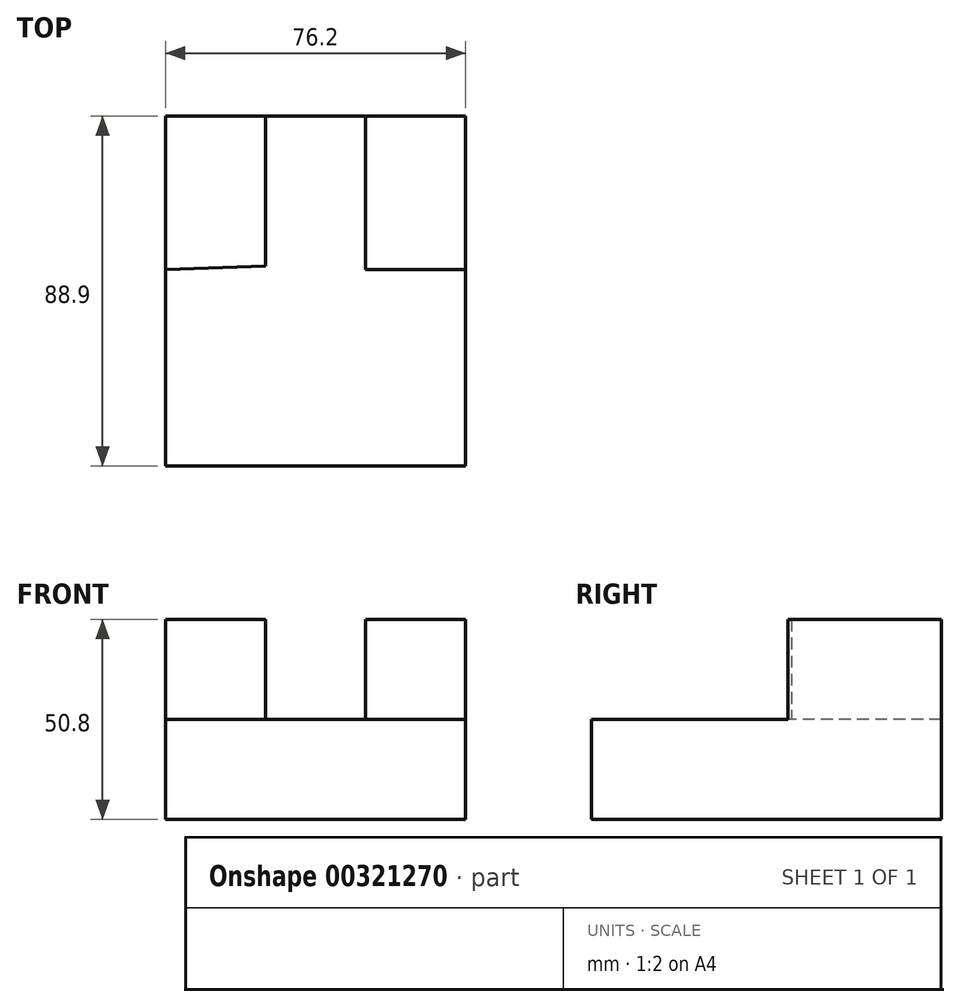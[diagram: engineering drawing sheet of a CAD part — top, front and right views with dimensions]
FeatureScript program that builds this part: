
annotation { "Feature Type Name" : "Feature", "Feature Type Description" : "" }
export const myFeature = defineFeature(function(context is Context, id is Id, definition is map)
    precondition{}
    {
        {
            var Q0;
            Q0=qCreatedBy(makeId("Right.planeOp"),FACE);
            var sketch = newSketch(context, id + "F0", { "sketchPlane" : qUnion([Q0])});
            skLineSegment(sketch, "E0", {"start": v(-49.86, -41.95) * mm, "end": v(39.04, -41.95) * mm});
            skLineSegment(sketch, "E1", {"start": v(-49.86, -41.95) * mm, "end": v(-49.86, -16.55) * mm});
            skLineSegment(sketch, "E2", {"start": v(-49.86, -16.55) * mm, "end": v(39.04, -16.55) * mm});
            skLineSegment(sketch, "E3", {"start": v(39.04, -16.55) * mm, "end": v(39.04, -41.95) * mm});
            skSolve(sketch);
        }
        {
            var Q0;
            Q0=makeQuery(id+"F0.imprint","IMPRINT",FACE,{"disambiguationData":[TD([[makeQuery(id+"F0.imprint","IMPRINT",EDGE,{"derivedFrom":sQuery(id+"F0.wireOp",EDGE,"E0")}),1.0]])]});
            extrude(context, id + "F1", {"entities" : qUnion([Q0]), "depth" : 76.2 * mm});
        }
        {
            var Q0;
            Q0=makeQuery(id+"F1.opExtrude","SWEPT_FACE",FACE,{"disambiguationData":[OSD([sQuery(id+"F0.wireOp",EDGE,"E2")])]});
            var sketch = newSketch(context, id + "F2", { "sketchPlane" : qUnion([Q0])});
            skLineSegment(sketch, "E4", {"start": v(0, 39.04) * mm, "end": v(25.4, 39.04) * mm});
            skLineSegment(sketch, "E5", {"start": v(25.4, 39.04) * mm, "end": v(25.4, 0.94) * mm});
            skLineSegment(sketch, "E6", {"start": v(25.4, 0.94) * mm, "end": v(0, 0) * mm});
            skLineSegment(sketch, "E7", {"start": v(0, 0) * mm, "end": v(0, 39.04) * mm});
            skSolve(sketch);
        }
        {
            var Q0;
            Q0=makeQuery(id+"F2.imprint","IMPRINT",FACE,{"disambiguationData":[TD([[makeQuery(id+"F2.imprint","IMPRINT",EDGE,{"derivedFrom":sQuery(id+"F2.wireOp",EDGE,"E4")}),1.0]])]});
            extrude(context, id + "F3", {"entities" : qUnion([Q0]), "operationType" : NewBodyOperationType.ADD, "depth" : 25.4 * mm});
        }
        {
            var Q0;
            Q0=makeQuery(id+"F1.opExtrude","SWEPT_FACE",FACE,{"disambiguationData":[OSD([sQuery(id+"F0.wireOp",EDGE,"E2")])]});
            var sketch = newSketch(context, id + "F4", { "sketchPlane" : qUnion([Q0])});
            skLineSegment(sketch, "E8", {"start": v(76.2, 39.04) * mm, "end": v(50.8, 39.04) * mm});
            skLineSegment(sketch, "E9", {"start": v(50.8, 39.04) * mm, "end": v(50.8, 0) * mm});
            skLineSegment(sketch, "E10", {"start": v(50.8, 0) * mm, "end": v(76.2, 0) * mm});
            skLineSegment(sketch, "E11", {"start": v(76.2, 0) * mm, "end": v(76.2, 39.04) * mm});
            skSolve(sketch);
        }
        {
            var Q0;
            Q0=makeQuery(id+"F4.imprint","IMPRINT",FACE,{"disambiguationData":[TD([[makeQuery(id+"F4.imprint","IMPRINT",EDGE,{"derivedFrom":sQuery(id+"F4.wireOp",EDGE,"E8")}),1.0]])]});
            extrude(context, id + "F5", {"entities" : qUnion([Q0]), "operationType" : NewBodyOperationType.ADD, "depth" : 25.4 * mm});
        }
    });
